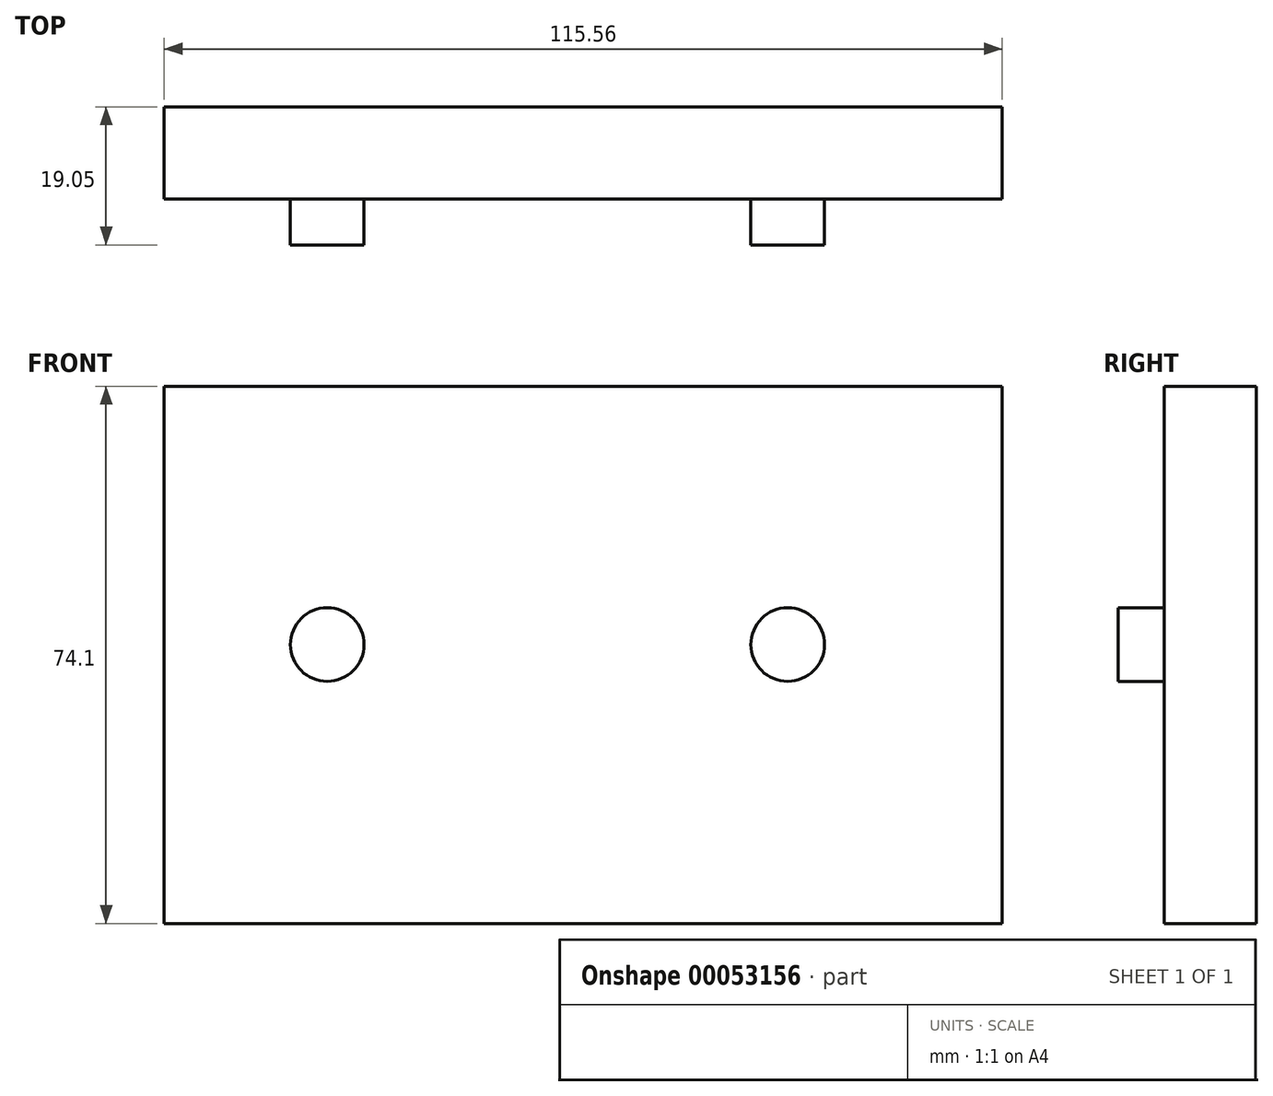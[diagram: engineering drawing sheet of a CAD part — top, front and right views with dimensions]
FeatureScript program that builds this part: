
annotation { "Feature Type Name" : "Feature", "Feature Type Description" : "" }
export const myFeature = defineFeature(function(context is Context, id is Id, definition is map)
    precondition{}
    {
        {
            var Q0;
            Q0=qCreatedBy(makeId("Front.planeOp"),FACE);
            var sketch = newSketch(context, id + "F0", { "sketchPlane" : qUnion([Q0])});
            skLineSegment(sketch, "E0.bottom", {"start": v(-54.23, 35.63) * mm, "end": v(61.33, 35.63) * mm});
            skLineSegment(sketch, "E0.top", {"start": v(-54.23, -38.47) * mm, "end": v(61.33, -38.47) * mm});
            skLineSegment(sketch, "E0.left", {"start": v(-54.23, 35.63) * mm, "end": v(-54.23, -38.47) * mm});
            skLineSegment(sketch, "E0.right", {"start": v(61.33, 35.63) * mm, "end": v(61.33, -38.47) * mm});
            skSolve(sketch);
        }
        {
            var Q0;
            Q0 = qSketchRegion(id + "F0", true);
            extrude(context, id + "F1", {"entities" : qUnion([Q0]), "oppositeDirection" : true, "depth" : 12.7 * mm});
        }
        {
            var Q0;
            Q0=qCreatedBy(makeId("Front.planeOp"),FACE);
            var sketch = newSketch(context, id + "F2", { "sketchPlane" : qUnion([Q0])});
            skLineSegment(sketch, "E1", {"start": v(-31.75, 0) * mm, "end": v(-31.75, 13.8) * mm, "construction": true});
            skLineSegment(sketch, "E2", {"start": v(31.75, 0) * mm, "end": v(31.75, 13.99) * mm, "construction": true});
            skCircle(sketch, "E3", {"center": v(-31.75, 0) * mm, "radius": 5.08 * mm});
            skCircle(sketch, "E4", {"center": v(31.75, 0) * mm, "radius": 5.08 * mm});
            skSolve(sketch);
        }
        {
            var Q0;
            Q0=makeQuery(id+"F2.imprint","IMPRINT",FACE,{"disambiguationData":[TD([[makeQuery(id+"F2.imprint","IMPRINT",EDGE,{"derivedFrom":sQuery(id+"F2.wireOp",EDGE,"E3")}),1.0]])]});
            var Q1;
            Q1=makeQuery(id+"F2.imprint","IMPRINT",FACE,{"disambiguationData":[TD([[makeQuery(id+"F2.imprint","IMPRINT",EDGE,{"derivedFrom":sQuery(id+"F2.wireOp",EDGE,"E4")}),1.0]])]});
            extrude(context, id + "F3", {"entities" : qUnion([Q0, Q1]), "operationType" : NewBodyOperationType.ADD, "depth" : 6.35 * mm});
        }
    });
